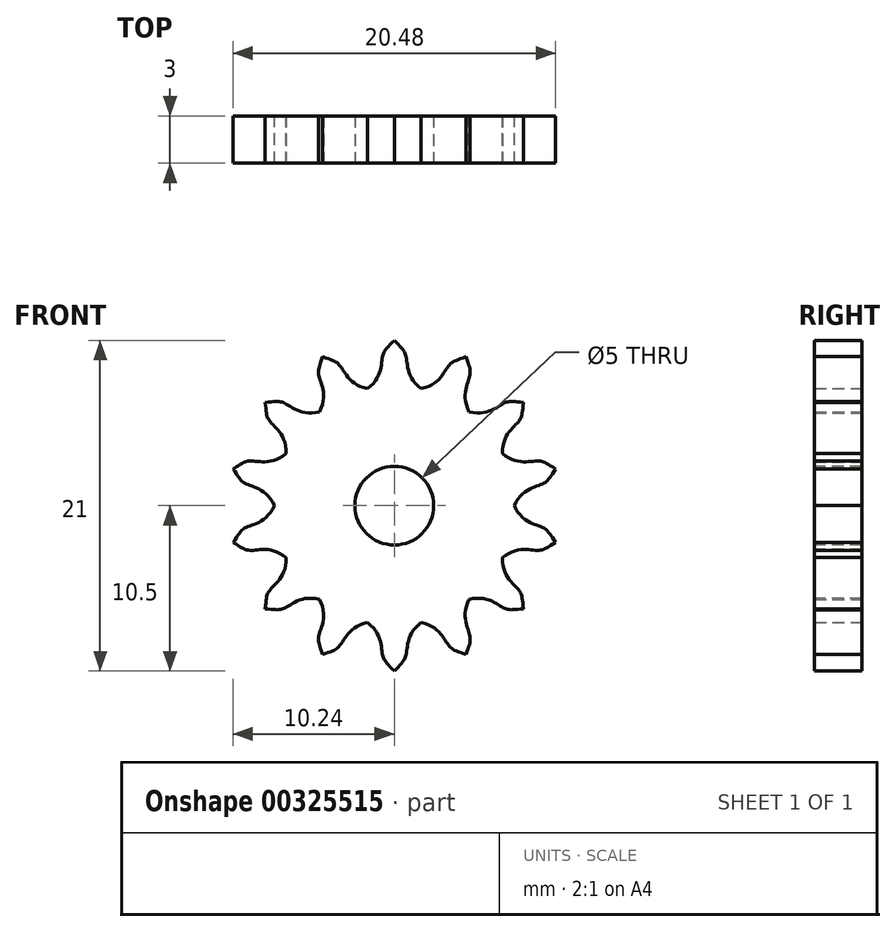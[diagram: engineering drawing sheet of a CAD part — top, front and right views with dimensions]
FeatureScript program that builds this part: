
annotation { "Feature Type Name" : "Feature", "Feature Type Description" : "" }
export const myFeature = defineFeature(function(context is Context, id is Id, definition is map)
    precondition{}
    {
        {
            var Q0;
            Q0=qCreatedBy(makeId("Front.planeOp"),FACE);
            var sketch = newSketch(context, id + "F0", { "sketchPlane" : qUnion([Q0])});
            skCircle(sketch, "E0", {"center": v(0, 0) * mm, "radius": 7.5 * mm, "construction": true});
            skCircle(sketch, "E1", {"center": v(0, 0) * mm, "radius": 10.5 * mm, "construction": true});
            skLineSegment(sketch, "E2", {"start": v(0, 10.5) * mm, "end": v(0, 7.5) * mm, "construction": true});
            skPoint(sketch, "E3", {"position": v(-2, 7.23) * mm});
            skPoint(sketch, "E4", {"position": v(2, 7.23) * mm});
            skFitSpline(sketch, "E5", {"points": [v(-2, 7.23) * mm, v(-0.75, 9.47) * mm, v(0, 10.5) * mm], "startDerivative": vector(6.4, 3.77) * mm, "endDerivative": vector(3.63, 3.72) * mm});
            skFitSpline(sketch, "E6.MirrorCS", {"points": [v(2, 7.23) * mm, v(0.75, 9.47) * mm, v(0, 10.5) * mm], "startDerivative": vector(-6.4, 3.77) * mm, "endDerivative": vector(-3.63, 3.72) * mm});
            skArc(sketch, "E7", {"start": v(-2, 7.23) * mm, "mid": v(0, -7.5) * mm, "end": v(2, 7.23) * mm});
            skCircle(sketch, "E8", {"center": v(0, 0) * mm, "radius": 8.91 * mm, "construction": true});
            skSolve(sketch);
        }
        {
            var Q0;
            Q0=qSketchRegion(id+"F0",true);
            extrude(context, id + "F1", {"entities" : qUnion([Q0]), "depth" : 3 * mm});
        }
        {
            var Q0;
            Q0=qCreatedBy(makeId("Right.planeOp"),FACE);
            var sketch = newSketch(context, id + "F2", { "sketchPlane" : qUnion([Q0])});
            skLineSegment(sketch, "E9", {"start": v(-21.19, 0) * mm, "end": v(26.28, 0) * mm, "construction": true});
            skSolve(sketch);
        }
        {
            var Q0;
            Q0=makeQuery(id+"F1.opExtrude","SWEPT_BODY",BODY,{"disambiguationData":[OSD([sQuery(id+"F0.wireOp",EDGE,"E5"),sQuery(id+"F0.wireOp",EDGE,"E6.MirrorCS"),sQuery(id+"F0.wireOp",EDGE,"E7")])]});
            var Q1;
            Q1=sQuery(id+"F2.wireOp",EDGE,"E9");
            circularPattern(context, id + "F3", {"operationType" : NewBodyOperationType.ADD, "entities" : qUnion([Q0]), "axis" : qUnion([Q1]), "angle" : 360 * degree, "instanceCount" : 14, "equalSpace" : true});
        }
        {
            var Q0;
            {var subQ0=makeQuery(id+"F1.opExtrude","CAP_FACE",FACE,{"disambiguationData":[OSD([sQuery(id+"F0.wireOp",EDGE,"E5"),sQuery(id+"F0.wireOp",EDGE,"E6.MirrorCS"),sQuery(id+"F0.wireOp",EDGE,"E7")])],"isStart":false});Q0=makeQuery(id+"F3.boolean.opBoolean","MERGE",FACE,{"derivedFrom":[subQ0,makeQuery(id+"F3.opPattern","COPY",FACE,{"derivedFrom":subQ0,"instanceName":"1"}),makeQuery(id+"F3.opPattern","COPY",FACE,{"derivedFrom":subQ0,"instanceName":"2"}),makeQuery(id+"F3.opPattern","COPY",FACE,{"derivedFrom":subQ0,"instanceName":"3"}),makeQuery(id+"F3.opPattern","COPY",FACE,{"derivedFrom":subQ0,"instanceName":"4"}),makeQuery(id+"F3.opPattern","COPY",FACE,{"derivedFrom":subQ0,"instanceName":"5"}),makeQuery(id+"F3.opPattern","COPY",FACE,{"derivedFrom":subQ0,"instanceName":"6"}),makeQuery(id+"F3.opPattern","COPY",FACE,{"derivedFrom":subQ0,"instanceName":"7"}),makeQuery(id+"F3.opPattern","COPY",FACE,{"derivedFrom":subQ0,"instanceName":"8"}),makeQuery(id+"F3.opPattern","COPY",FACE,{"derivedFrom":subQ0,"instanceName":"9"}),makeQuery(id+"F3.opPattern","COPY",FACE,{"derivedFrom":subQ0,"instanceName":"10"}),makeQuery(id+"F3.opPattern","COPY",FACE,{"derivedFrom":subQ0,"instanceName":"11"}),makeQuery(id+"F3.opPattern","COPY",FACE,{"derivedFrom":subQ0,"instanceName":"12"}),makeQuery(id+"F3.opPattern","COPY",FACE,{"derivedFrom":subQ0,"instanceName":"13"}),makeQuery(id+"F3.opPattern","COPY",FACE,{"derivedFrom":subQ0,"instanceName":"14"})]});}
            var sketch = newSketch(context, id + "F4", { "sketchPlane" : qUnion([Q0])});
            skCircle(sketch, "E10", {"center": v(0, 0) * mm, "radius": 2.5 * mm});
            skSolve(sketch);
        }
        {
            var Q0;
            Q0=qSketchRegion(id+"F4",true);
            extrude(context, id + "F5", {"entities" : qUnion([Q0]), "operationType" : NewBodyOperationType.REMOVE, "endBound" : BoundingType.UP_TO_NEXT, "oppositeDirection" : true, "depth" : 25 * mm});
        }
    });
